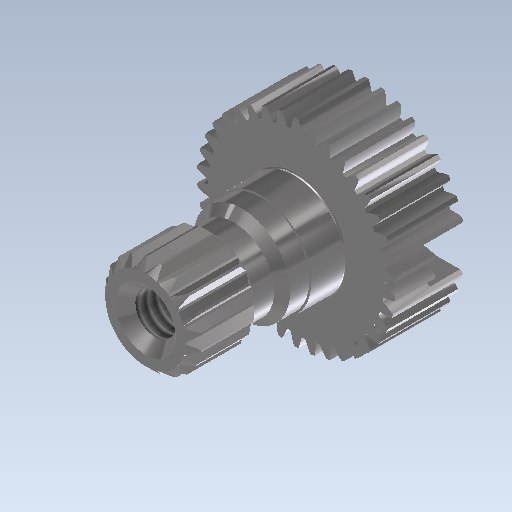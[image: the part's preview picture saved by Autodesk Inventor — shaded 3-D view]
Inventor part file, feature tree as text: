
AUTODESK INVENTOR PART (.ipt)
format: ipt  version: 2020 (Build 240168000, 168)  size: 531,456 bytes
history: native  units: mm (DEFAULTED — no unit token found)
features: sketch x7, extrude x4, plane x3, other x3, chamfer x3, revolve x1, fillet x1, hole x1, pattern_circular x1
ambient origin geometry x8: Origin, YZ Plane, XZ Plane, XY Plane, X Axis, Y Axis, Z Axis, Center Point
bodies: Solid1 (feature_tree)
feature tree (24):
  extrude  "Extrusion1"  Depth=10.0mm TaperAngle=0.0deg
  plane  "Work Plane2"
  plane  "Work Plane8"
  plane  "Work Plane9"
  other  "Цилиндрическое зубчатое зацепление"
  revolve  "Вращение1"
  fillet  "Сопряжение1"  Radius=9.5mm
  chamfer  "Фаска1"  Distance=10.0mm
  hole  "Отверстие1"  [1 undecoded]
  chamfer  "Фаска2"  [1 undecoded]
  extrude  "Выдавливание2"  TaperAngle=0.0deg  [1 undecoded]
  extrude  "Выдавливание3"  Depth=6.0mm
  extrude  "Выдавливание4"  Depth=6.0mm
  pattern_circular  "Круговой массив1"  [2 undecoded]
  chamfer  "Фаска3"  Distance=7.5mm
  sketch  "Sketch1"  dims[d0=9.865mm d1=3.5mm d2=0.0mm d3=9.5mm d4=10.0mm d5=0.0mm]
  sketch  "Sketch2"  dims[d16=6.0mm d17=0.0mm d34=0.826735mm d39=0.0mm d41=0.0mm d43=6.0mm d46=6.0mm d47=0.0mm d48=0.0mm d49=7.5mm d50=4.8mm d51=4.0mm d52=4.8mm d53=5.0mm d55=1.75mm d56=1.0mm d57=4.1mm d58=3.4mm d59=90.0deg d60=0.1mm d61=0.4mm d62=2.0mm d63=45.0deg d64=2.013mm d65=11.0mm d66=3.4mm d67=4.5mm d68=14.3117mm d69=11.0mm d70=20.594885mm d71=0.2mm d72=2.0mm d73=45.0deg d74=7.0mm d75=1.0mm d76=0.0mm d77=6.0mm d78=2.0mm d79=1.5mm d80=0.0mm d82=3.141593mm d86=0.05mm d87=0.05mm d88=0.1mm d89=3.5mm d90=0.0mm d91=200.0mm d92=360.0deg d94=0.5mm d95=2.0mm d96=45.0deg]
  other  "Srf1"
  sketch  "Эскиз3"
  sketch  "Эскиз4"
  sketch  "Эскиз5"
  sketch  "Эскиз6"
  sketch  "Эскиз7"
  other  "Средний диаметр"
note: 5 required parameter values undecoded (feature->parameter linkage not recoverable at this tier; creation-order binding heuristic only, values carry confidence <= 0.55)
